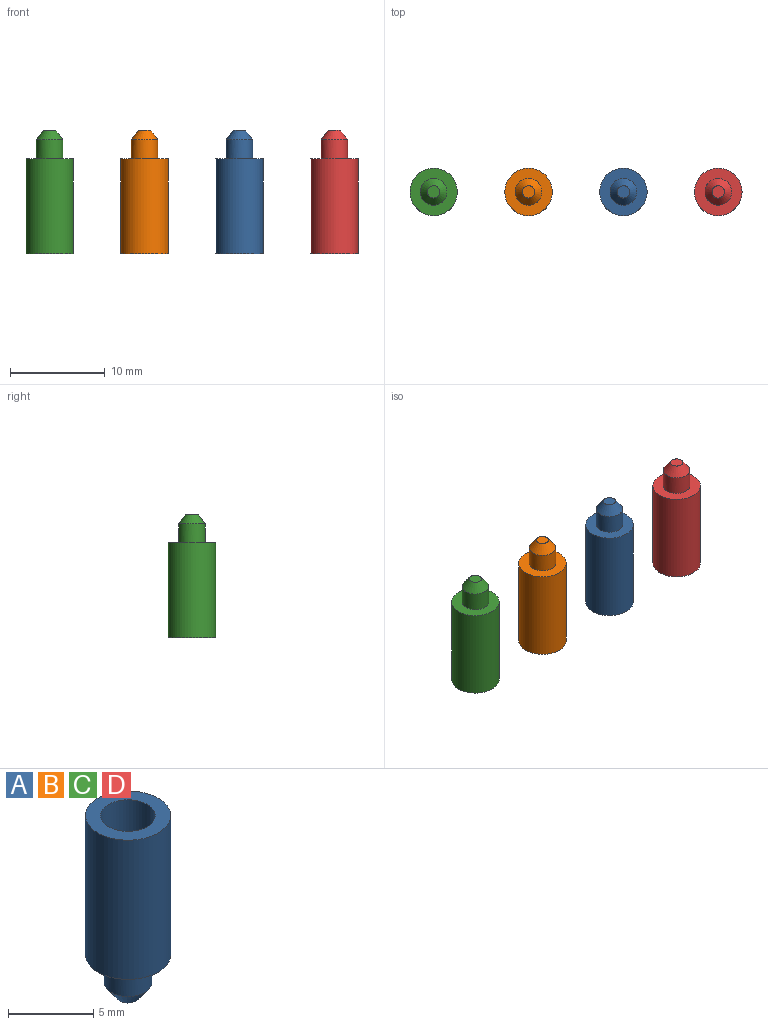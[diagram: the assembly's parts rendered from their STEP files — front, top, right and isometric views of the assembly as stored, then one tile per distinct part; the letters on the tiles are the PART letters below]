
ASSEMBLY  parts=4 mates=3
PART A: 8 faces, bbox 5x5x13 mm
  f0: plane 3.2x3.2mm, normal (0,0,1), area 8mm2, adj f1
  f1: cylinder r=1.6mm len=4mm, axis (0,0,1), area 40.2mm2, adj f0,f2
  f2: plane 5x5mm, normal (0,0,1), area 11.6mm2, adj f1,f3
  f3: cylinder r=2.5mm len=10mm, axis (0,0,1), area 157.1mm2, adj f2,f4
  f4: plane 5x5mm, normal (0,0,-1), area 13.5mm2, adj f3,f5
  f5: cylinder r=1.4mm len=2.8mm, axis (0,0,1), area 17.6mm2, adj f4,f7
  f6: plane 1.3x1.3mm, normal (0,0,-1), area 1.3mm2, adj f7
  f7: cone r=1.4mm half-angle=36.9deg, axis (0,0,1), area 8.1mm2, adj f5,f6
PART B: same geometry as A
PART C: same geometry as A
PART D: same geometry as A
PLACE A rot(axis=(-1,0,0),180deg) t=(20,0,10)mm
PLACE B rot(axis=(-1,0,0),180deg) t=(10,0,10)mm
PLACE C rot(axis=(-1,0,0),180deg) t=(0,0,10)mm fixed
PLACE D rot(axis=(-1,0,0),180deg) t=(30,0,10)mm
MATE fastened D.f1 <-> C.f2  axis (0,0,-1) through (30,0,0)mm
MATE fastened A.f1 <-> C.f2  axis (0,0,-1) through (20,0,0)mm
MATE fastened C.f1 <-> B.f2  axis (0,0,-1) through (0,0,0)mm
